# Revit family: Projector-DLP-Panasonic-1_Chip-Full_Brightness-Longer_Lasting_Laser_Performance-PT-FRZ55_SeriesX
name_source: partatom
category: Communication Devices
units: mm (PartAtom-declared; Revit-internal decimal feet)

## family parameters
Cut with Voids When Loaded = Yes
Host = Face
Maintain Annotation Orientation = No
OmniClass Number = 23.85.10.17.11.21
OmniClass Title = Data/Multi/Media Projectors
Part Type = Normal
Room Calculation Point = No
Round Connector Dimension = Use Diameter
Shared = No

## types (1)
- PT-FRZ55
    352_mm = High_Ceiling_Height : 352_mm
    392_mm = High_Ceiling_Height : 392_mm
    432_mm = High_Ceiling_Height : 432_mm
    A_Supplied_Max = 0.6892
    A_Supplied_Min = 0.6892
    Body Depth = 460 mm  [stored 1.50919 ft]
    Brightness Economy = 4000 lm
    Brightness Full = 5000 lm
    Ceiling Distance = 100 mm  [stored 0.328084 ft]
    Chip Diagonal = 17 mm
    Chip Quantity = 1
    Clearance Value = 500 mm  [stored 1.64042 ft]
    Const Length Projector Pan Handle = 2000 mm  [stored 6.56168 ft]
    Const Length Projector Panning Base = 1000 mm  [stored 3.28084 ft]
    Contrast Ratio = 20000
    Date Last Modified = 2020/10/14
    Default Elevation = 0 mm  [stored 0 ft]
    Depth = 481 mm
    Description = 5,000 Lumens, 16:10 Aspect Ratio, WUXGA, Projector, PT-FRZ55
    Equipment Abbreviation = LVP
    Family Version = 1.0.0
    HDMI In = HDMI 19-pin x 2 Compatible with HDCP 2.3, Deep Color, 4K/60p signal input*6, CEC supported
    Heat Load Active = 1587.00 Btu/h
    Height = 168 mm  [stored 0.551181 ft]
    LAN = RJ‑45 x 1 for network connection, PJLink (class 2) compatible, 10Base‑T/100Base‑TX, Art-Net compatible
    Lamp Life Economy = 24000
    Lamp Life Full = 20000
    Lamp Quantity = 2
    Lamp Type = Laser Diode
    Lens Type = Integrated
    Manufacturer = Panasonic
    Market = Commercial
    Max Air Exhaust Volume = 285.00 CFM
    Model = PT-FRZ55
    Model Disclaimer = Contact Panasonic for more information
    Motorized Zoom = No
    Must be Level = No
    Noise in High Mode = 32
    Noise in Low Mode = 27
    P Type = 55
    Panasonic Logo Material = Paint - Panasonic Logo
    Part Description = 5,000 Lumens, 16:10 Aspect Ratio, WUXGA, Projector, PT-FRZ55
    Part Number = PT-FRZ55
    Power Active = 465 W
    Power Standby Eco = 1 W
    Power Standby Normal = 10 W
    Product Documentation Link = https://bizpartner.panasonic.net
    Product Material = Plastic - Panasonic Black
    Product Page URL = https://panasonic.net
    Provide Feedback = https://www.surveymonkey.com
    Resolution Horizontal = 1920
    Resolution Vertical = 1200
    Technology = DLP™ chip x 1, DLP™ projection system
    Temperature Max = 113 °F
    Temperature Min = 32 °F
    Total Rated Watts = 465 W
    URL = http://panasonic.net
    Weight = 36.20 lb
    Width = 498 mm  [stored 1.63386 ft]

note: [stored X ft] marks values corroborated as IEEE doubles in the binary element streams (Revit-internal decimal feet)

## geometry (parser evidence)
native form markers: Blend x2, Sweep x5
no freeform markers — native parametric forms only
